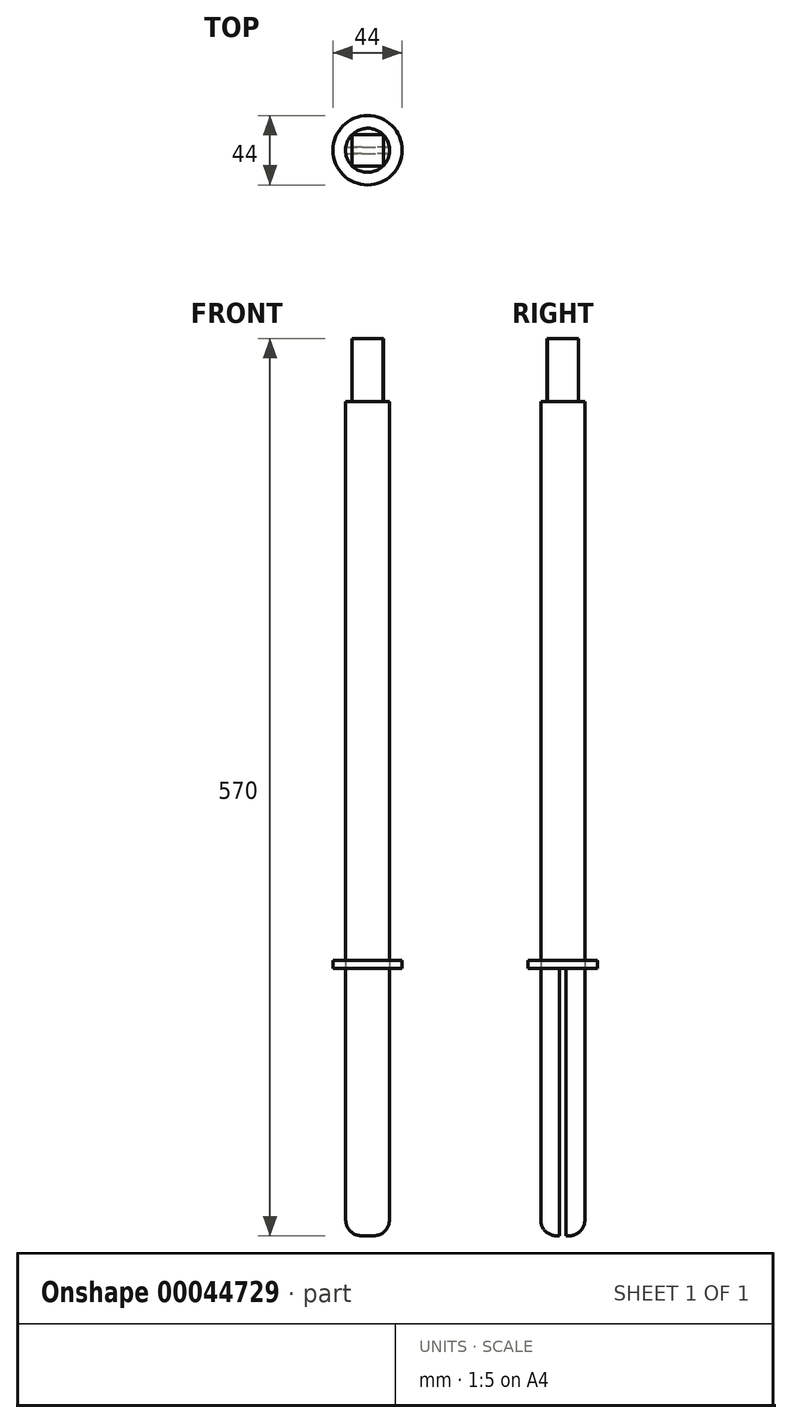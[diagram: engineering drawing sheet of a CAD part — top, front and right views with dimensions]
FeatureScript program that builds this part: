
annotation { "Feature Type Name" : "Feature", "Feature Type Description" : "" }
export const myFeature = defineFeature(function(context is Context, id is Id, definition is map)
    precondition{}
    {
        {
            var Q0;
            Q0=qCreatedBy(makeId("Top.planeOp"),FACE);
            cPlane(context, id + "F0", {"entities" : qUnion([Q0]), "cplaneType" : CPlaneType.OFFSET, "offset" : 275 * mm, "width" : 150 * mm, "height" : 150 * mm});
        }
        {
            var Q0;
            Q0=qCreatedBy(id+"F0.planeOp",FACE);
            var sketch = newSketch(context, id + "F1", { "sketchPlane" : qUnion([Q0])});
            skCircle(sketch, "E0", {"center": v(154, 0) * mm, "radius": 22 * mm});
            skSolve(sketch);
        }
        {
            var Q0;
            Q0=qSketchRegion(id+"F1",true);
            extrude(context, id + "F2", {"entities" : qUnion([Q0]), "depth" : 5 * mm});
        }
        {
            var Q0;
            Q0=makeQuery(id+"F2.opExtrude","CAP_FACE",FACE,{"disambiguationData":[OSD([sQuery(id+"F1.wireOp",EDGE,"E0")])],"isStart":false});
            var sketch = newSketch(context, id + "F3", { "sketchPlane" : qUnion([Q0])});
            skCircle(sketch, "E1", {"center": v(154, 0) * mm, "radius": 14 * mm});
            skSolve(sketch);
        }
        {
            var Q0;
            Q0=qSketchRegion(id+"F3",true);
            extrude(context, id + "F4", {"entities" : qUnion([Q0]), "depth" : 355 * mm, "hasSecondDirection" : true, "secondDirectionOppositeDirection" : true, "secondDirectionDepth" : 175 * mm});
        }
        {
            var Q0;
            Q0=makeQuery(id+"F4.opExtrude","CAP_FACE",FACE,{"disambiguationData":[OSD([sQuery(id+"F3.wireOp",EDGE,"E1")])],"isStart":false});
            var sketch = newSketch(context, id + "F5", { "sketchPlane" : qUnion([Q0])});
            skPoint(sketch, "E2.rect.middle", {"position": v(154, 0) * mm});
            skLineSegment(sketch, "E3.rect.bottom", {"start": v(163.8, 10) * mm, "end": v(144.2, 10) * mm});
            skLineSegment(sketch, "E3.rect.top", {"start": v(163.8, -10) * mm, "end": v(144.2, -10) * mm});
            skLineSegment(sketch, "E3.rect.left", {"start": v(164, 9.8) * mm, "end": v(164, -9.8) * mm});
            skLineSegment(sketch, "E3.rect.right", {"start": v(144, 9.8) * mm, "end": v(144, 9.8) * mm});
            skLineSegment(sketch, "E4", {"start": v(144.2, 10) * mm, "end": v(144, 9.8) * mm});
            skPoint(sketch, "E5.orphan", {"position": v(144, 10) * mm});
            skLineSegment(sketch, "E6", {"start": v(163.8, 10) * mm, "end": v(164, 9.8) * mm});
            skPoint(sketch, "E7.orphan", {"position": v(164, 10) * mm});
            skLineSegment(sketch, "E8", {"start": v(144, 9.8) * mm, "end": v(144.2, -10) * mm});
            skPoint(sketch, "E9.orphan", {"position": v(144, -10) * mm});
            skLineSegment(sketch, "E10", {"start": v(164, -9.8) * mm, "end": v(163.8, -10) * mm});
            skPoint(sketch, "E11.orphan", {"position": v(164, -10) * mm});
            skSolve(sketch);
        }
        {
            var Q0;
            Q0=qSketchRegion(id+"F5",true);
            extrude(context, id + "F6", {"entities" : qUnion([Q0]), "depth" : 40 * mm});
        }
        {
            var Q0;
            {var subQ0=sQuery(id+"F3.wireOp",EDGE,"E1");Q0=makeQuery(id+"F4.boolean.opBoolean","SPLIT",EDGE,{"disambiguationData":[TD([makeQuery(id+"F2g9KFsyuyMbi0D_0.opExtrude","CAP_FACE",FACE,{"disambiguationData":[OSD([sQuery(id+"FciuOZmgVB1eZRo_0.wireOp",EDGE,"0a2e5e20-2bbe-4bfa-95bb-bc97e7c899b3"),sQuery(id+"FciuOZmgVB1eZRo_0.wireOp",EDGE,"18282615-4ef4-492b-b24f-8010f7ceb41a"),sQuery(id+"FciuOZmgVB1eZRo_0.wireOp",EDGE,"a34203a6-c0ce-494d-b41a-1cdfb6cc057e"),sQuery(id+"FciuOZmgVB1eZRo_0.wireOp",EDGE,"158d94a9-51ae-45e2-92bf-82838fa154c7"),sQuery(id+"FciuOZmgVB1eZRo_0.wireOp",EDGE,"b453020b-6489-4288-9455-f6b60d525ef1"),sQuery(id+"FciuOZmgVB1eZRo_0.wireOp",EDGE,"6f74799e-f0b4-41c7-ab6a-f4070288c4b2"),sQuery(id+"FciuOZmgVB1eZRo_0.wireOp",EDGE,"1a2e0718-e9a4-46fd-a18b-da8c078026d3"),sQuery(id+"FciuOZmgVB1eZRo_0.wireOp",EDGE,"1d4100d9-dc35-425b-add8-cc2fe18c1581"),sQuery(id+"FciuOZmgVB1eZRo_0.wireOp",EDGE,"eae650be-55d2-421f-b5fb-913f3ac7ef57")])],"isStart":true})])],"derivedFrom":makeQuery(id+"F4.opExtrude","CAP_EDGE",EDGE,{"disambiguationData":[OSD([subQ0])],"isStart":true})});}
            var Q1;
            {var subQ0=sQuery(id+"F3.wireOp",EDGE,"E1");Q1=makeQuery(id+"F4.boolean.opBoolean","SPLIT",EDGE,{"disambiguationData":[TD([makeQuery(id+"F2g9KFsyuyMbi0D_0.opExtrude","CAP_FACE",FACE,{"disambiguationData":[OSD([sQuery(id+"FciuOZmgVB1eZRo_0.wireOp",EDGE,"0a2e5e20-2bbe-4bfa-95bb-bc97e7c899b3"),sQuery(id+"FciuOZmgVB1eZRo_0.wireOp",EDGE,"18282615-4ef4-492b-b24f-8010f7ceb41a"),sQuery(id+"FciuOZmgVB1eZRo_0.wireOp",EDGE,"a34203a6-c0ce-494d-b41a-1cdfb6cc057e"),sQuery(id+"FciuOZmgVB1eZRo_0.wireOp",EDGE,"158d94a9-51ae-45e2-92bf-82838fa154c7"),sQuery(id+"FciuOZmgVB1eZRo_0.wireOp",EDGE,"b453020b-6489-4288-9455-f6b60d525ef1"),sQuery(id+"FciuOZmgVB1eZRo_0.wireOp",EDGE,"6f74799e-f0b4-41c7-ab6a-f4070288c4b2"),sQuery(id+"FciuOZmgVB1eZRo_0.wireOp",EDGE,"1a2e0718-e9a4-46fd-a18b-da8c078026d3"),sQuery(id+"FciuOZmgVB1eZRo_0.wireOp",EDGE,"1d4100d9-dc35-425b-add8-cc2fe18c1581"),sQuery(id+"FciuOZmgVB1eZRo_0.wireOp",EDGE,"eae650be-55d2-421f-b5fb-913f3ac7ef57")])],"isStart":false})])],"derivedFrom":makeQuery(id+"F4.opExtrude","CAP_EDGE",EDGE,{"disambiguationData":[OSD([subQ0])],"isStart":true})});}
            fillet(context, id + "F7", {"entities" : qUnion([Q0, Q1]), "radius" : 10 * mm, "tangentPropagation" : true, "allowEdgeOverflow" : false});
        }
        {
            var Q0;
            Q0=qCreatedBy(makeId("Right.planeOp"),FACE);
            cPlane(context, id + "F8", {"entities" : qUnion([Q0]), "cplaneType" : CPlaneType.OFFSET, "offset" : 175 * mm, "width" : 150 * mm, "height" : 150 * mm});
        }
        {
            var Q0;
            Q0=qCreatedBy(id+"F8.planeOp",FACE);
            var sketch = newSketch(context, id + "F9", { "sketchPlane" : qUnion([Q0])});
            skLineSegment(sketch, "E12.bottom", {"start": v(2, 275) * mm, "end": v(-2, 275) * mm});
            skLineSegment(sketch, "E12.top", {"start": v(2, 100) * mm, "end": v(-2, 100) * mm});
            skLineSegment(sketch, "E12.left", {"start": v(2, 275) * mm, "end": v(2, 100) * mm});
            skLineSegment(sketch, "E12.right", {"start": v(-2, 275) * mm, "end": v(-2, 100) * mm});
            skSolve(sketch);
        }
        {
            var Q0;
            Q0 = qSketchRegion(id + "F9", true);
            extrude(context, id + "F10", {"entities" : qUnion([Q0]), "operationType" : NewBodyOperationType.REMOVE, "endBound" : BoundingType.THROUGH_ALL, "oppositeDirection" : true, "depth" : 25 * mm, "hasSecondDirection" : true, "secondDirectionOppositeDirection" : false, "secondDirectionDepth" : 25 * mm});
        }
    });
